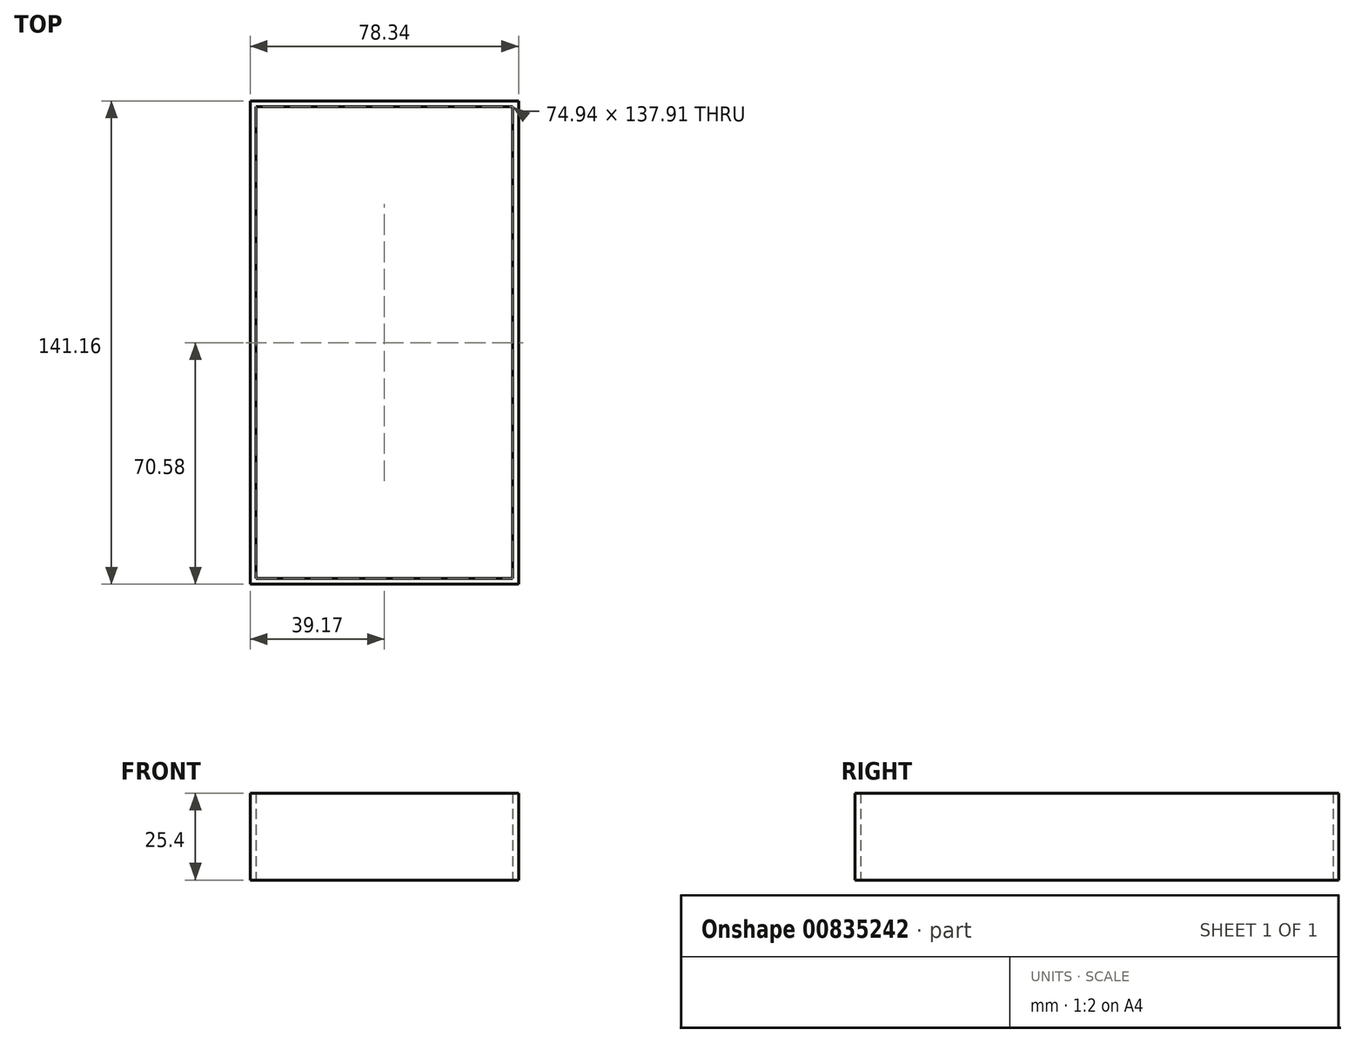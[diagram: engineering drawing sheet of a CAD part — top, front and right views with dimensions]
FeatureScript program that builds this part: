
annotation { "Feature Type Name" : "Feature", "Feature Type Description" : "" }
export const myFeature = defineFeature(function(context is Context, id is Id, definition is map)
    precondition{}
    {
        {
            var Q0;
            Q0=qCreatedBy(makeId("Top.planeOp"),FACE);
            var sketch = newSketch(context, id + "F0", { "sketchPlane" : qUnion([Q0])});
            skLineSegment(sketch, "E0.bottom", {"start": v(39.17, 70.58) * mm, "end": v(-39.17, 70.58) * mm});
            skLineSegment(sketch, "E0.top", {"start": v(39.17, -70.58) * mm, "end": v(-39.17, -70.58) * mm});
            skLineSegment(sketch, "E0.left", {"start": v(39.17, 70.58) * mm, "end": v(39.17, -70.58) * mm});
            skLineSegment(sketch, "E0.right", {"start": v(-39.17, 70.58) * mm, "end": v(-39.17, -70.58) * mm});
            skPoint(sketch, "E0.middle", {"position": v(0, 0) * mm});
            skLineSegment(sketch, "E1.bottom", {"start": v(37.47, 68.95) * mm, "end": v(-37.47, 68.95) * mm});
            skLineSegment(sketch, "E1.top", {"start": v(37.47, -68.95) * mm, "end": v(-37.47, -68.95) * mm});
            skLineSegment(sketch, "E1.left", {"start": v(37.47, 68.95) * mm, "end": v(37.47, -68.95) * mm});
            skLineSegment(sketch, "E1.right", {"start": v(-37.47, 68.95) * mm, "end": v(-37.47, -68.95) * mm});
            skSolve(sketch);
        }
        {
            var Q0;
            Q0 = qSketchRegion(id + "F0", true);
            extrude(context, id + "F1", {"entities" : qUnion([Q0]), "depth" : 25.4 * mm, "offsetDistance" : 25.4 * mm});
        }
    });
